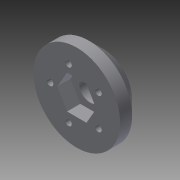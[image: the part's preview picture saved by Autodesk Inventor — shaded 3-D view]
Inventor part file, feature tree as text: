
AUTODESK INVENTOR PART (.ipt)
format: ipt  version: 2014 SP2 (Build 180246200, 246)  size: 140,800 bytes
history: native  units: mm
features: extrude x4, sketch x3, chamfer x1
ambient origin geometry x8: Origin, YZ Plane, XZ Plane, XY Plane, X Axis, Y Axis, Z Axis, Center Point
bodies: Solid1 (feature_tree)
feature tree (8):
  extrude  "Extrusion1"  Depth=22.2mm
  extrude  "Extrusion2"  Depth=2.7mm
  extrude  "Extrusion3"  Depth=5.5mm
  extrude  "Extrusion4"  Depth=5.5mm
  chamfer  "Chamfer1"  Distance=5.0mm
  sketch  "Sketch1"  dims[d0=36.0mm d1=22.2mm]
  sketch  "Sketch3"  dims[d2=2.7mm d3=2.7mm]
  sketch  "Sketch4"  dims[d4=2.7mm d5=2.7mm d6=2.7mm d7=5.0mm d8=0.0mm d9=30.0mm d14=6.0mm d15=0.0mm d23=14.0mm d24=5.5mm d25=0.0mm d26=9.0mm d27=9.0mm d28=0.0mm d29=3.0mm d30=2.0mm d31=45.0deg]
